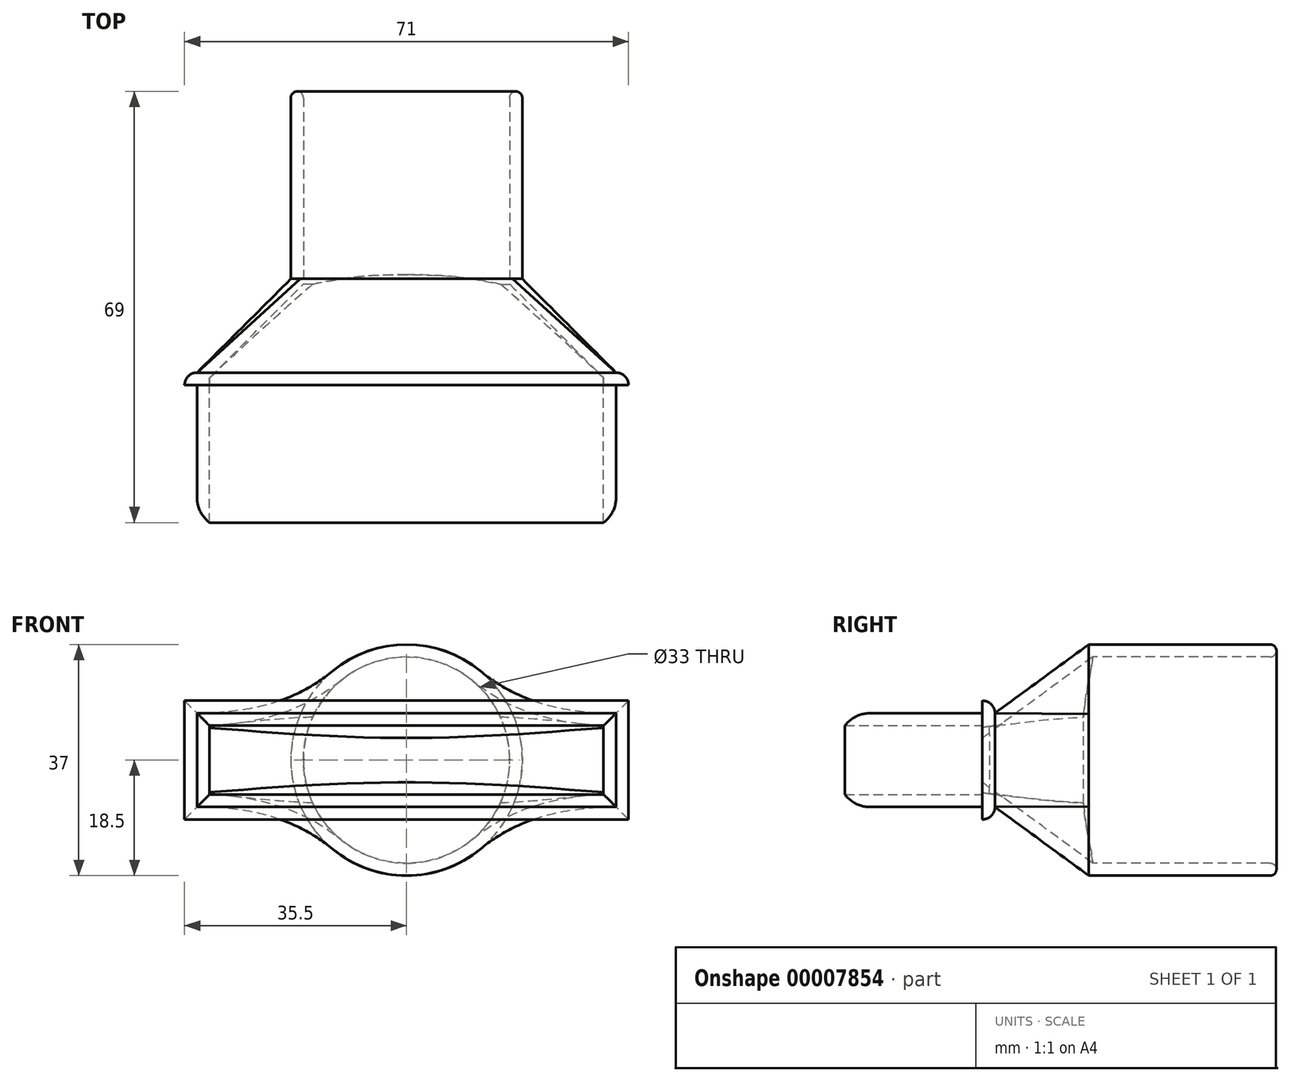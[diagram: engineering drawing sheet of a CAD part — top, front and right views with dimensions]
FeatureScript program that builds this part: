
annotation { "Feature Type Name" : "Feature", "Feature Type Description" : "" }
export const myFeature = defineFeature(function(context is Context, id is Id, definition is map)
    precondition{}
    {
        {
            var Q0;
            Q0=qCreatedBy(makeId("Front.planeOp"),FACE);
            var sketch = newSketch(context, id + "F0", { "sketchPlane" : qUnion([Q0])});
            skCircle(sketch, "E0", {"center": v(0, 0) * mm, "radius": 18.5 * mm});
            skLineSegment(sketch, "E1.rect.bottom", {"start": v(33.5, -7.5) * mm, "end": v(-33.5, -7.5) * mm});
            skLineSegment(sketch, "E1.rect.top", {"start": v(33.5, 7.5) * mm, "end": v(-33.5, 7.5) * mm});
            skLineSegment(sketch, "E1.rect.left", {"start": v(33.5, -7.5) * mm, "end": v(33.5, 7.5) * mm});
            skLineSegment(sketch, "E1.rect.right", {"start": v(-33.5, -7.5) * mm, "end": v(-33.5, 7.5) * mm});
            skLineSegment(sketch, "E2.0", {"start": v(35.5, -9.5) * mm, "end": v(35.5, 9.5) * mm});
            skLineSegment(sketch, "E2.1", {"start": v(35.5, -9.5) * mm, "end": v(-35.5, -9.5) * mm});
            skLineSegment(sketch, "E2.2", {"start": v(-35.5, -9.5) * mm, "end": v(-35.5, 9.5) * mm});
            skLineSegment(sketch, "E2.3", {"start": v(35.5, 9.5) * mm, "end": v(-35.5, 9.5) * mm});
            skCircle(sketch, "E3", {"center": v(0, 0) * mm, "radius": 7.5 * mm});
            skLineSegment(sketch, "E4", {"start": v(0, 18.5) * mm, "end": v(0, -18.5) * mm, "construction": true});
            skLineSegment(sketch, "E5", {"start": v(0, 7.5) * mm, "end": v(0, -7.5) * mm, "construction": true});
            skSolve(sketch);
        }
        {
            var Q0;
            {var subQ0=sQuery(id+"F0.wireOp",EDGE,"E1.rect.left");Q0=makeQuery(id+"F0.imprint","IMPRINT",FACE,{"disambiguationData":[TD([[makeQuery(id+"F0.imprint","IMPRINT",EDGE,{"derivedFrom":subQ0}),1.0]])]});}
            var Q1;
            {var subQ1=sQuery(id+"F0.wireOp",EDGE,"E1.rect.top");var subQ5=sQuery(id+"F0.wireOp",EDGE,"E0");var subQ6=makeQuery(id+"F0.imprint","INTERSECT",VERTEX,{"disambiguationData":[OD(1.0)],"derivedFrom":[subQ5,subQ1]});Q1=makeQuery(id+"F0.imprint","IMPRINT",FACE,{"disambiguationData":[TD([[makeQuery(id+"F0.imprint","IMPRINT",EDGE,{"disambiguationData":[TD([[subQ6,-1.0]])],"derivedFrom":subQ5}),1.0]])]});}
            var Q2;
            {var subQ1=sQuery(id+"F0.wireOp",EDGE,"E1.rect.top");var subQ5=sQuery(id+"F0.wireOp",EDGE,"E0");var subQ6=makeQuery(id+"F0.imprint","INTERSECT",VERTEX,{"disambiguationData":[OD(0.0)],"derivedFrom":[subQ5,subQ1]});Q2=makeQuery(id+"F0.imprint","IMPRINT",FACE,{"disambiguationData":[TD([[makeQuery(id+"F0.imprint","IMPRINT",EDGE,{"disambiguationData":[TD([[subQ6,1.0]])],"derivedFrom":subQ5}),1.0]])]});}
            var Q3;
            {var subQ0=sQuery(id+"F0.wireOp",EDGE,"E1.rect.right");Q3=makeQuery(id+"F0.imprint","IMPRINT",FACE,{"disambiguationData":[TD([[makeQuery(id+"F0.imprint","IMPRINT",EDGE,{"derivedFrom":subQ0}),-1.0]])]});}
            var Q4;
            {var subQ0=sQuery(id+"F0.wireOp",EDGE,"E3");var subQ2=makeQuery(id+"F0.imprint","INTERSECT",VERTEX,{"derivedFrom":[sQuery(id+"F0.wireOp",EDGE,"E1.rect.bottom"),subQ0]});Q4=makeQuery(id+"F0.imprint","IMPRINT",FACE,{"disambiguationData":[TD([[makeQuery(id+"F0.imprint","IMPRINT",EDGE,{"disambiguationData":[TD([[subQ2,1.0]])],"derivedFrom":subQ0}),1.0]])]});}
            extrude(context, id + "F1", {"entities" : qUnion([Q0, Q1, Q2, Q3, Q4]), "depth" : 30 * mm, "hasSecondDirection" : true, "secondDirectionOppositeDirection" : false, "secondDirectionDepth" : 5 * mm});
        }
        {
            var Q0;
            {var subQ0=sQuery(id+"F0.wireOp",EDGE,"E3");var subQ2=makeQuery(id+"F0.imprint","INTERSECT",VERTEX,{"derivedFrom":[sQuery(id+"F0.wireOp",EDGE,"E1.rect.bottom"),subQ0]});Q0=makeQuery(id+"F0.imprint","IMPRINT",FACE,{"disambiguationData":[TD([[makeQuery(id+"F0.imprint","IMPRINT",EDGE,{"disambiguationData":[TD([[subQ2,1.0]])],"derivedFrom":subQ0}),1.0]])]});}
            var Q1;
            {var subQ1=sQuery(id+"F0.wireOp",EDGE,"E1.rect.top");var subQ5=sQuery(id+"F0.wireOp",EDGE,"E0");var subQ6=makeQuery(id+"F0.imprint","INTERSECT",VERTEX,{"disambiguationData":[OD(0.0)],"derivedFrom":[subQ5,subQ1]});Q1=makeQuery(id+"F0.imprint","IMPRINT",FACE,{"disambiguationData":[TD([[makeQuery(id+"F0.imprint","IMPRINT",EDGE,{"disambiguationData":[TD([[subQ6,1.0]])],"derivedFrom":subQ5}),1.0]])]});}
            var Q2;
            {var subQ0=sQuery(id+"F0.wireOp",EDGE,"E2.1");var subQ1=sQuery(id+"F0.wireOp",EDGE,"E0");var subQ3=makeQuery(id+"F0.imprint","INTERSECT",VERTEX,{"disambiguationData":[OD(0.0)],"derivedFrom":[subQ1,subQ0]});Q2=makeQuery(id+"F0.imprint","IMPRINT",FACE,{"disambiguationData":[TD([[makeQuery(id+"F0.imprint","IMPRINT",EDGE,{"disambiguationData":[TD([[subQ3,1.0]])],"derivedFrom":subQ1}),1.0]])]});}
            var Q3;
            {var subQ0=sQuery(id+"F0.wireOp",EDGE,"E2.3");var subQ1=sQuery(id+"F0.wireOp",EDGE,"E0");var subQ3=makeQuery(id+"F0.imprint","INTERSECT",VERTEX,{"disambiguationData":[OD(0.0)],"derivedFrom":[subQ1,subQ0]});Q3=makeQuery(id+"F0.imprint","IMPRINT",FACE,{"disambiguationData":[TD([[makeQuery(id+"F0.imprint","IMPRINT",EDGE,{"disambiguationData":[TD([[subQ3,-1.0]])],"derivedFrom":subQ1}),1.0]])]});}
            var Q4;
            {var subQ1=sQuery(id+"F0.wireOp",EDGE,"E1.rect.top");var subQ5=sQuery(id+"F0.wireOp",EDGE,"E0");var subQ6=makeQuery(id+"F0.imprint","INTERSECT",VERTEX,{"disambiguationData":[OD(1.0)],"derivedFrom":[subQ5,subQ1]});Q4=makeQuery(id+"F0.imprint","IMPRINT",FACE,{"disambiguationData":[TD([[makeQuery(id+"F0.imprint","IMPRINT",EDGE,{"disambiguationData":[TD([[subQ6,-1.0]])],"derivedFrom":subQ5}),1.0]])]});}
            var Q5;
            {var subQ0=sQuery(id+"F0.wireOp",EDGE,"E2.1");var subQ1=sQuery(id+"F0.wireOp",EDGE,"E0");var subQ3=makeQuery(id+"F0.imprint","INTERSECT",VERTEX,{"disambiguationData":[OD(0.0)],"derivedFrom":[subQ1,subQ0]});Q5=makeQuery(id+"F0.imprint","IMPRINT",FACE,{"disambiguationData":[TD([[makeQuery(id+"F0.imprint","IMPRINT",EDGE,{"disambiguationData":[TD([[subQ3,-1.0]])],"derivedFrom":subQ1}),1.0]])]});}
            var Q6;
            {var subQ0=sQuery(id+"F0.wireOp",EDGE,"E2.3");var subQ1=sQuery(id+"F0.wireOp",EDGE,"E0");var subQ3=makeQuery(id+"F0.imprint","INTERSECT",VERTEX,{"disambiguationData":[OD(0.0)],"derivedFrom":[subQ1,subQ0]});Q6=makeQuery(id+"F0.imprint","IMPRINT",FACE,{"disambiguationData":[TD([[makeQuery(id+"F0.imprint","IMPRINT",EDGE,{"disambiguationData":[TD([[subQ3,1.0]])],"derivedFrom":subQ1}),1.0]])]});}
            extrude(context, id + "F2", {"entities" : qUnion([Q0, Q1, Q2, Q3, Q4, Q5, Q6]), "oppositeDirection" : true, "depth" : 40 * mm, "hasSecondDirection" : true, "secondDirectionOppositeDirection" : true, "secondDirectionDepth" : 10 * mm});
        }
        {
            var Q0;
            {var subQ4=sQuery(id+"F0.wireOp",EDGE,"E1.rect.left");Q0=makeQuery(id+"F0.imprint","IMPRINT",FACE,{"disambiguationData":[TD([[makeQuery(id+"F0.imprint","IMPRINT",EDGE,{"derivedFrom":subQ4}),-1.0]])]});}
            var Q1;
            {var subQ0=sQuery(id+"F0.wireOp",EDGE,"E2.3");var subQ1=sQuery(id+"F0.wireOp",EDGE,"E0");var subQ3=makeQuery(id+"F0.imprint","INTERSECT",VERTEX,{"disambiguationData":[OD(0.0)],"derivedFrom":[subQ1,subQ0]});Q1=makeQuery(id+"F0.imprint","IMPRINT",FACE,{"disambiguationData":[TD([[makeQuery(id+"F0.imprint","IMPRINT",EDGE,{"disambiguationData":[TD([[subQ3,1.0]])],"derivedFrom":subQ1}),1.0]])]});}
            var Q2;
            {var subQ0=sQuery(id+"F0.wireOp",EDGE,"E2.1");var subQ1=sQuery(id+"F0.wireOp",EDGE,"E0");var subQ3=makeQuery(id+"F0.imprint","INTERSECT",VERTEX,{"disambiguationData":[OD(0.0)],"derivedFrom":[subQ1,subQ0]});Q2=makeQuery(id+"F0.imprint","IMPRINT",FACE,{"disambiguationData":[TD([[makeQuery(id+"F0.imprint","IMPRINT",EDGE,{"disambiguationData":[TD([[subQ3,1.0]])],"derivedFrom":subQ1}),1.0]])]});}
            var Q3;
            {var subQ6=sQuery(id+"F0.wireOp",EDGE,"E1.rect.right");Q3=makeQuery(id+"F0.imprint","IMPRINT",FACE,{"disambiguationData":[TD([[makeQuery(id+"F0.imprint","IMPRINT",EDGE,{"derivedFrom":subQ6}),1.0]])]});}
            extrude(context, id + "F3", {"entities" : qUnion([Q0, Q1, Q2, Q3]), "depth" : 7 * mm, "hasSecondDirection" : true, "secondDirectionOppositeDirection" : false, "secondDirectionDepth" : 5 * mm});
        }
        {
            var Q0;
            Q0=makeQuery(id+"F1.opExtrude","CAP_FACE",FACE,{"disambiguationData":[OSD([sQuery(id+"F0.wireOp",EDGE,"E1.rect.bottom"),sQuery(id+"F0.wireOp",EDGE,"E1.rect.top"),sQuery(id+"F0.wireOp",EDGE,"E1.rect.left"),sQuery(id+"F0.wireOp",EDGE,"E1.rect.right")])],"isStart":true});
            var sketch = newSketch(context, id + "F4", { "sketchPlane" : qUnion([Q0])});
            skLineSegment(sketch, "E6.0", {"start": v(-33.5, -7.5) * mm, "end": v(-33.5, 7.5) * mm});
            skLineSegment(sketch, "E6.1", {"start": v(33.5, -7.5) * mm, "end": v(33.5, 7.5) * mm});
            skLineSegment(sketch, "E6.2", {"start": v(-33.5, -7.5) * mm, "end": v(33.5, -7.5) * mm});
            skLineSegment(sketch, "E6.3", {"start": v(-33.5, 7.5) * mm, "end": v(33.5, 7.5) * mm});
            skSolve(sketch);
        }
        {
            var Q0;
            Q0=makeQuery(id+"F2.opExtrude","CAP_FACE",FACE,{"disambiguationData":[OSD([sQuery(id+"F0.wireOp",EDGE,"E0")])],"isStart":true});
            var sketch = newSketch(context, id + "F5", { "sketchPlane" : qUnion([Q0])});
            skPoint(sketch, "E7.rect.middle", {"position": v(0, 0) * mm});
            skArc(sketch, "E8", {"start": v(16.96, -7.4) * mm, "mid": v(18.5, 0) * mm, "end": v(16.96, 7.4) * mm});
            skArc(sketch, "E9", {"start": v(16.96, 7.4) * mm, "mid": v(0, 18.5) * mm, "end": v(-16.96, 7.4) * mm});
            skArc(sketch, "E10", {"start": v(-16.96, -7.4) * mm, "mid": v(0, -18.5) * mm, "end": v(16.96, -7.4) * mm});
            skArc(sketch, "E11", {"start": v(-16.96, 7.4) * mm, "mid": v(-18.5, 0) * mm, "end": v(-16.96, -7.4) * mm});
            skPoint(sketch, "E7.rect.right.end.orphan", {"position": v(-16.96, 7.4) * mm});
            skPoint(sketch, "E7.rect.right.start.orphan", {"position": v(-17.18, -7.5) * mm});
            skPoint(sketch, "E7.rect.left.end.orphan", {"position": v(17.18, 7.5) * mm});
            skPoint(sketch, "E7.rect.left.start.orphan", {"position": v(16.96, -7.4) * mm});
            skSolve(sketch);
        }
        {
            var Q0;
            Q0=makeQuery(id+"F4.imprint","IMPRINT",FACE,{"disambiguationData":[TD([[makeQuery(id+"F4.imprint","IMPRINT",EDGE,{"derivedFrom":sQuery(id+"F4.wireOp",EDGE,"E6.0")}),-1.0]])]});
            var Q1;
            Q1=makeQuery(id+"F5.imprint","IMPRINT",FACE,{"disambiguationData":[TD([[makeQuery(id+"F5.imprint","IMPRINT",EDGE,{"derivedFrom":sQuery(id+"F5.wireOp",EDGE,"E8")}),1.0]])]});
            loft(context, id + "F6", {"operationType" : NewBodyOperationType.ADD, "sheetProfilesArray" : [{ "sheetProfileEntities" : qUnion([Q0]) }, { "sheetProfileEntities" : qUnion([Q1]) }]});
        }
        {
            var Q0;
            Q0=makeQuery(id+"F2.opExtrude","CAP_FACE",FACE,{"disambiguationData":[OSD([sQuery(id+"F0.wireOp",EDGE,"E0")])],"isStart":false});
            var Q1;
            Q1=makeQuery(id+"F1.opExtrude","CAP_FACE",FACE,{"disambiguationData":[OSD([sQuery(id+"F0.wireOp",EDGE,"E1.rect.bottom"),sQuery(id+"F0.wireOp",EDGE,"E1.rect.top"),sQuery(id+"F0.wireOp",EDGE,"E1.rect.left"),sQuery(id+"F0.wireOp",EDGE,"E1.rect.right")])],"isStart":false});
            shell(context, id + "F7", {"entities" : qUnion([Q0, Q1]), "thickness" : 2 * mm});
        }
        {
            var Q0;
            Q0=makeQuery(id+"F1.opExtrude","CAP_EDGE",EDGE,{"disambiguationData":[OSD([sQuery(id+"F0.wireOp",EDGE,"E1.rect.right")])],"isStart":false});
            var Q1;
            Q1=makeQuery(id+"F1.opExtrude","CAP_EDGE",EDGE,{"disambiguationData":[OSD([sQuery(id+"F0.wireOp",EDGE,"E1.rect.bottom")])],"isStart":false});
            var Q2;
            Q2=makeQuery(id+"F1.opExtrude","CAP_EDGE",EDGE,{"disambiguationData":[OSD([sQuery(id+"F0.wireOp",EDGE,"E1.rect.left")])],"isStart":false});
            var Q3;
            Q3=makeQuery(id+"F1.opExtrude","CAP_EDGE",EDGE,{"disambiguationData":[OSD([sQuery(id+"F0.wireOp",EDGE,"E1.rect.top")])],"isStart":false});
            fillet(context, id + "F8", {"entities" : qUnion([Q0, Q1, Q2, Q3]), "radius" : 5 * mm, "tangentPropagation" : true, "allowEdgeOverflow" : false});
        }
        {
            var Q0;
            Q0=makeQuery(id+"F7.opShell","OFFSET_EDGE",EDGE,{"disambiguationData":[OSD([sQuery(id+"F0.wireOp",EDGE,"E0")])]});
            var Q1;
            Q1=makeQuery(id+"F2.opExtrude","CAP_EDGE",EDGE,{"disambiguationData":[OSD([sQuery(id+"F0.wireOp",EDGE,"E0")])],"isStart":false});
            fillet(context, id + "F9", {"entities" : qUnion([Q0, Q1]), "radius" : 1 * mm, "tangentPropagation" : true, "allowEdgeOverflow" : false});
        }
        {
            var Q0;
            Q0=makeQuery(id+"F3.opExtrude","CAP_EDGE",EDGE,{"disambiguationData":[OSD([sQuery(id+"F0.wireOp",EDGE,"E2.0")])],"isStart":true});
            var Q1;
            Q1=makeQuery(id+"F3.opExtrude","CAP_EDGE",EDGE,{"disambiguationData":[OSD([sQuery(id+"F0.wireOp",EDGE,"E2.1")])],"isStart":true});
            var Q2;
            Q2=makeQuery(id+"F3.opExtrude","CAP_EDGE",EDGE,{"disambiguationData":[OSD([sQuery(id+"F0.wireOp",EDGE,"E2.2")])],"isStart":true});
            var Q3;
            Q3=makeQuery(id+"F3.opExtrude","CAP_EDGE",EDGE,{"disambiguationData":[OSD([sQuery(id+"F0.wireOp",EDGE,"E2.3")])],"isStart":true});
            fillet(context, id + "F10", {"entities" : qUnion([Q0, Q1, Q2, Q3]), "radius" : 2 * mm, "tangentPropagation" : true, "allowEdgeOverflow" : false});
        }
    });
